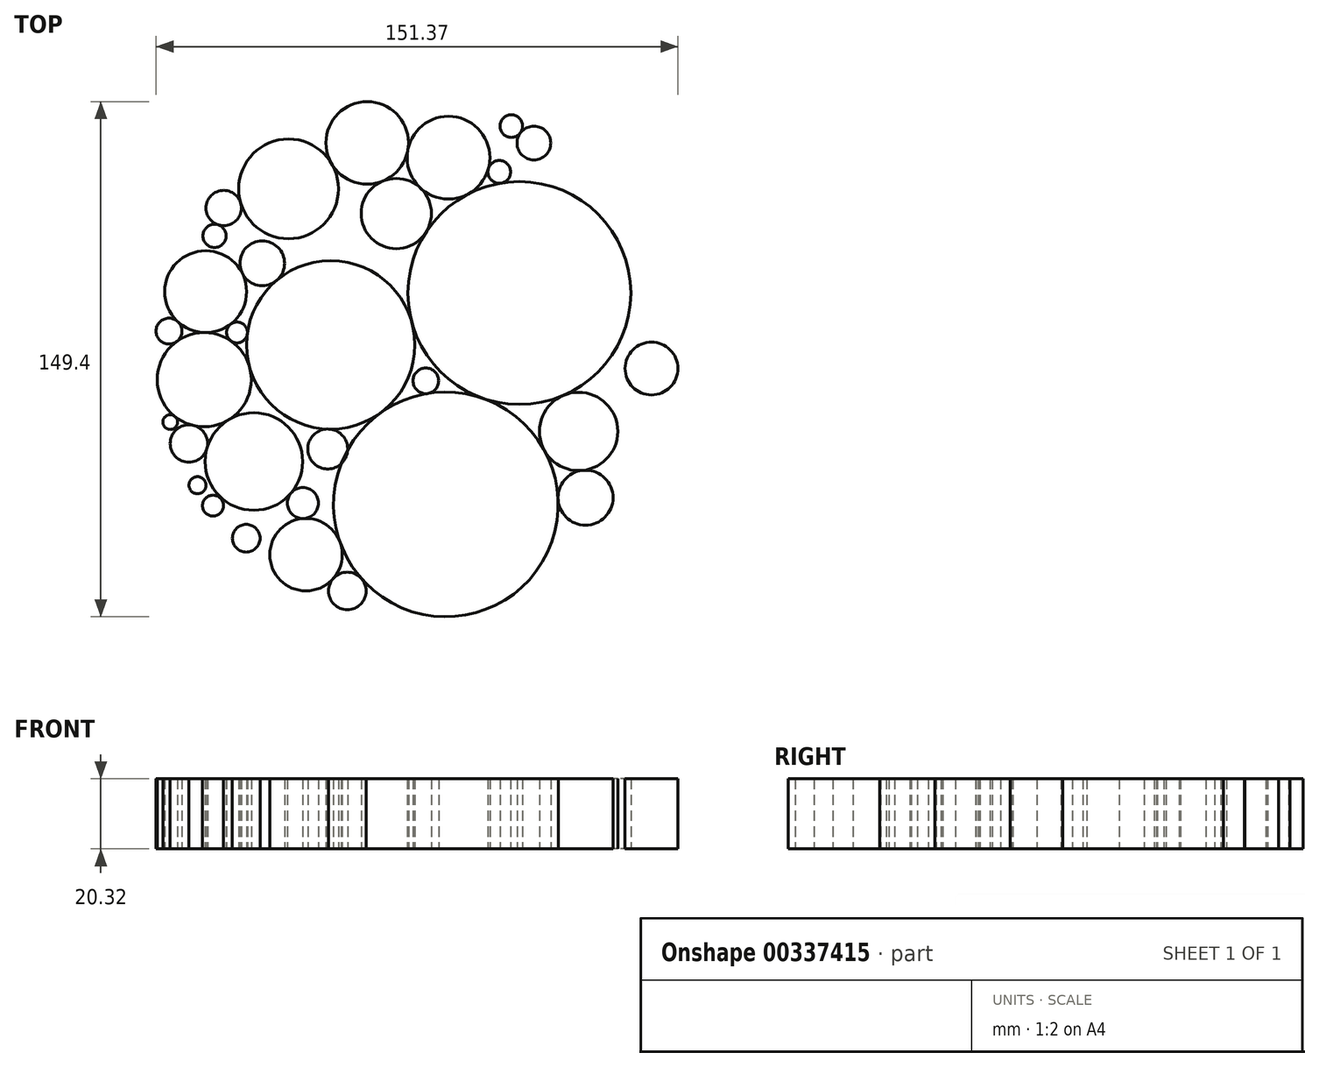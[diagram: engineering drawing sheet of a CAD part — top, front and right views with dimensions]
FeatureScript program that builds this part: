
annotation { "Feature Type Name" : "Feature", "Feature Type Description" : "" }
export const myFeature = defineFeature(function(context is Context, id is Id, definition is map)
    precondition{}
    {
        {
            var Q0;
            Q0=qCreatedBy(makeId("Top.planeOp"),FACE);
            var sketch = newSketch(context, id + "F0", { "sketchPlane" : qUnion([Q0])});
            skCircle(sketch, "E0", {"center": v(0, 0) * mm, "radius": 75.93 * mm});
            skCircle(sketch, "E1", {"center": v(-37.07, 49.03) * mm, "radius": 14.46 * mm});
            skCircle(sketch, "E2", {"center": v(-55.87, 43.47) * mm, "radius": 5.14 * mm});
            skCircle(sketch, "E3", {"center": v(-61.11, 19.2) * mm, "radius": 11.87 * mm});
            skCircle(sketch, "E4", {"center": v(-58.54, 35.4) * mm, "radius": 3.36 * mm});
            skCircle(sketch, "E5", {"center": v(-14.26, 62.36) * mm, "radius": 11.96 * mm});
            skCircle(sketch, "E6", {"center": v(29.88, 18.82) * mm, "radius": 32.32 * mm});
            skCircle(sketch, "E7", {"center": v(9.32, 58.1) * mm, "radius": 12 * mm});
            skCircle(sketch, "E8", {"center": v(34.08, 62.33) * mm, "radius": 4.9 * mm});
            skCircle(sketch, "E9", {"center": v(27.53, 67.23) * mm, "radius": 3.29 * mm});
            skCircle(sketch, "E10", {"center": v(24.05, 53.96) * mm, "radius": 3.3 * mm});
            skCircle(sketch, "E11", {"center": v(8.55, -42.49) * mm, "radius": 32.6 * mm});
            skCircle(sketch, "E12", {"center": v(47.06, -21.33) * mm, "radius": 11.35 * mm});
            skCircle(sketch, "E13", {"center": v(49.07, -40.55) * mm, "radius": 7.98 * mm});
            skCircle(sketch, "E14", {"center": v(68.2, -3.07) * mm, "radius": 7.66 * mm});
            skCircle(sketch, "E15", {"center": v(-61.53, -6.3) * mm, "radius": 13.64 * mm});
            skCircle(sketch, "E16", {"center": v(-47.13, -30.05) * mm, "radius": 14.14 * mm});
            skCircle(sketch, "E17", {"center": v(-66, -24.83) * mm, "radius": 5.42 * mm});
            skCircle(sketch, "E18", {"center": v(-24.84, 3.79) * mm, "radius": 24.42 * mm});
            skCircle(sketch, "E19", {"center": v(-5.83, 41.88) * mm, "radius": 10.19 * mm});
            skCircle(sketch, "E20", {"center": v(-44.71, 27.45) * mm, "radius": 6.48 * mm});
            skCircle(sketch, "E21", {"center": v(-25.7, -26.41) * mm, "radius": 5.8 * mm});
            skCircle(sketch, "E22", {"center": v(2.74, -6.64) * mm, "radius": 3.72 * mm});
            skCircle(sketch, "E23", {"center": v(-32.9, -42.1) * mm, "radius": 4.5 * mm});
            skCircle(sketch, "E24", {"center": v(-32, -57.07) * mm, "radius": 10.5 * mm});
            skCircle(sketch, "E25", {"center": v(-49.36, -52.3) * mm, "radius": 4.02 * mm});
            skCircle(sketch, "E26", {"center": v(-58.99, -42.83) * mm, "radius": 3.03 * mm});
            skCircle(sketch, "E27", {"center": v(-63.5, -36.92) * mm, "radius": 2.47 * mm});
            skCircle(sketch, "E28", {"center": v(-71.4, -18.6) * mm, "radius": 2.14 * mm});
            skCircle(sketch, "E29", {"center": v(-71.76, 7.77) * mm, "radius": 3.75 * mm});
            skCircle(sketch, "E30", {"center": v(-52.04, 7.4) * mm, "radius": 3.02 * mm});
            skCircle(sketch, "E31", {"center": v(-20.03, -67.59) * mm, "radius": 5.44 * mm});
            skCircle(sketch, "E32", {"center": v(14.35, -71.34) * mm, "radius": 3.16 * mm});
            skSolve(sketch);
        }
        {
            var Q0;
            Q0=makeQuery(id+"F0.imprint","IMPRINT",FACE,{"disambiguationData":[TD([[makeQuery(id+"F0.imprint","IMPRINT",EDGE,{"derivedFrom":sQuery(id+"F0.wireOp",EDGE,"E14")}),1.0]])]});
            var Q1;
            Q1=makeQuery(id+"F0.imprint","IMPRINT",FACE,{"disambiguationData":[TD([[makeQuery(id+"F0.imprint","IMPRINT",EDGE,{"derivedFrom":sQuery(id+"F0.wireOp",EDGE,"E25")}),1.0]])]});
            var Q2;
            Q2=makeQuery(id+"F0.imprint","IMPRINT",FACE,{"disambiguationData":[TD([[makeQuery(id+"F0.imprint","IMPRINT",EDGE,{"derivedFrom":sQuery(id+"F0.wireOp",EDGE,"E26")}),1.0]])]});
            var Q3;
            Q3=makeQuery(id+"F0.imprint","IMPRINT",FACE,{"disambiguationData":[TD([[makeQuery(id+"F0.imprint","IMPRINT",EDGE,{"derivedFrom":sQuery(id+"F0.wireOp",EDGE,"E27")}),1.0]])]});
            var Q4;
            Q4=makeQuery(id+"F0.imprint","IMPRINT",FACE,{"disambiguationData":[TD([[makeQuery(id+"F0.imprint","IMPRINT",EDGE,{"derivedFrom":sQuery(id+"F0.wireOp",EDGE,"E32")}),1.0]])]});
            var Q5;
            {var subQ0=sQuery(id+"F0.wireOp",EDGE,"E2");var subQ1=makeQuery(id+"F0.imprint","INTERSECT",VERTEX,{"derivedFrom":[sQuery(id+"F0.wireOp",EDGE,"E0"),subQ0]});Q5=makeQuery(id+"F0.imprint","IMPRINT",FACE,{"disambiguationData":[TD([[makeQuery(id+"F0.imprint","IMPRINT",EDGE,{"disambiguationData":[TD([[subQ1,1.0]])],"derivedFrom":subQ0}),1.0]])]});}
            var Q6;
            {var subQ0=sQuery(id+"F0.wireOp",EDGE,"E8");var subQ1=makeQuery(id+"F0.imprint","INTERSECT",VERTEX,{"derivedFrom":[sQuery(id+"F0.wireOp",EDGE,"E0"),subQ0]});Q6=makeQuery(id+"F0.imprint","IMPRINT",FACE,{"disambiguationData":[TD([[makeQuery(id+"F0.imprint","IMPRINT",EDGE,{"disambiguationData":[TD([[subQ1,-1.0]])],"derivedFrom":subQ0}),1.0]])]});}
            var Q7;
            {var subQ0=sQuery(id+"F0.wireOp",EDGE,"E9");var subQ1=makeQuery(id+"F0.imprint","INTERSECT",VERTEX,{"derivedFrom":[sQuery(id+"F0.wireOp",EDGE,"E0"),subQ0]});Q7=makeQuery(id+"F0.imprint","IMPRINT",FACE,{"disambiguationData":[TD([[makeQuery(id+"F0.imprint","IMPRINT",EDGE,{"disambiguationData":[TD([[subQ1,-1.0]])],"derivedFrom":subQ0}),1.0]])]});}
            var Q8;
            {var subQ0=sQuery(id+"F0.wireOp",EDGE,"E28");var subQ1=makeQuery(id+"F0.imprint","INTERSECT",VERTEX,{"derivedFrom":[sQuery(id+"F0.wireOp",EDGE,"E0"),subQ0]});Q8=makeQuery(id+"F0.imprint","IMPRINT",FACE,{"disambiguationData":[TD([[makeQuery(id+"F0.imprint","IMPRINT",EDGE,{"disambiguationData":[TD([[subQ1,1.0]])],"derivedFrom":subQ0}),1.0]])]});}
            var Q9;
            {var subQ0=sQuery(id+"F0.wireOp",EDGE,"E1");var subQ1=makeQuery(id+"F0.imprint","INTERSECT",VERTEX,{"derivedFrom":[sQuery(id+"F0.wireOp",EDGE,"E0"),subQ0]});Q9=makeQuery(id+"F0.imprint","IMPRINT",FACE,{"disambiguationData":[TD([[makeQuery(id+"F0.imprint","IMPRINT",EDGE,{"disambiguationData":[TD([[subQ1,1.0]])],"derivedFrom":subQ0}),1.0]])]});}
            var Q10;
            {var subQ0=sQuery(id+"F0.wireOp",EDGE,"E17");var subQ1=makeQuery(id+"F0.imprint","INTERSECT",VERTEX,{"derivedFrom":[sQuery(id+"F0.wireOp",EDGE,"E0"),subQ0]});Q10=makeQuery(id+"F0.imprint","IMPRINT",FACE,{"disambiguationData":[TD([[makeQuery(id+"F0.imprint","IMPRINT",EDGE,{"disambiguationData":[TD([[subQ1,1.0]])],"derivedFrom":subQ0}),1.0]])]});}
            var Q11;
            {var subQ0=sQuery(id+"F0.wireOp",EDGE,"E29");var subQ1=makeQuery(id+"F0.imprint","INTERSECT",VERTEX,{"derivedFrom":[sQuery(id+"F0.wireOp",EDGE,"E0"),subQ0]});Q11=makeQuery(id+"F0.imprint","IMPRINT",FACE,{"disambiguationData":[TD([[makeQuery(id+"F0.imprint","IMPRINT",EDGE,{"disambiguationData":[TD([[subQ1,1.0]])],"derivedFrom":subQ0}),1.0]])]});}
            var Q12;
            {var subQ0=sQuery(id+"F0.wireOp",EDGE,"E31");var subQ1=makeQuery(id+"F0.imprint","INTERSECT",VERTEX,{"derivedFrom":[sQuery(id+"F0.wireOp",EDGE,"E11"),subQ0]});Q12=makeQuery(id+"F0.imprint","IMPRINT",FACE,{"disambiguationData":[TD([[makeQuery(id+"F0.imprint","IMPRINT",EDGE,{"disambiguationData":[TD([[subQ1,-1.0]])],"derivedFrom":subQ0}),1.0]])]});}
            var Q13;
            {var subQ0=sQuery(id+"F0.wireOp",EDGE,"E5");var subQ1=makeQuery(id+"F0.imprint","INTERSECT",VERTEX,{"derivedFrom":[sQuery(id+"F0.wireOp",EDGE,"E0"),subQ0]});Q13=makeQuery(id+"F0.imprint","IMPRINT",FACE,{"disambiguationData":[TD([[makeQuery(id+"F0.imprint","IMPRINT",EDGE,{"disambiguationData":[TD([[subQ1,-1.0]])],"derivedFrom":subQ0}),1.0]])]});}
            var Q14;
            {var subQ0=sQuery(id+"F0.wireOp",EDGE,"E24");var subQ1=makeQuery(id+"F0.imprint","INTERSECT",VERTEX,{"derivedFrom":[sQuery(id+"F0.wireOp",EDGE,"E11"),subQ0]});Q14=makeQuery(id+"F0.imprint","IMPRINT",FACE,{"disambiguationData":[TD([[makeQuery(id+"F0.imprint","IMPRINT",EDGE,{"disambiguationData":[TD([[subQ1,-1.0]])],"derivedFrom":subQ0}),1.0]])]});}
            var Q15;
            {var subQ0=sQuery(id+"F0.wireOp",EDGE,"E3");var subQ4=makeQuery(id+"F0.imprint","INTERSECT",VERTEX,{"derivedFrom":[sQuery(id+"F0.wireOp",EDGE,"E0"),subQ0]});Q15=makeQuery(id+"F0.imprint","IMPRINT",FACE,{"disambiguationData":[TD([[makeQuery(id+"F0.imprint","IMPRINT",EDGE,{"disambiguationData":[TD([[subQ4,1.0]])],"derivedFrom":subQ0}),1.0]])]});}
            var Q16;
            {var subQ10=sQuery(id+"F0.wireOp",EDGE,"E32");Q16=makeQuery(id+"F0.imprint","IMPRINT",FACE,{"disambiguationData":[TD([[makeQuery(id+"F0.imprint","IMPRINT",EDGE,{"derivedFrom":subQ10}),-1.0]])]});}
            var Q17;
            {var subQ0=sQuery(id+"F0.wireOp",EDGE,"E20");var subQ1=makeQuery(id+"F0.imprint","INTERSECT",VERTEX,{"derivedFrom":[sQuery(id+"F0.wireOp",EDGE,"E3"),subQ0]});Q17=makeQuery(id+"F0.imprint","IMPRINT",FACE,{"disambiguationData":[TD([[makeQuery(id+"F0.imprint","IMPRINT",EDGE,{"disambiguationData":[TD([[subQ1,-1.0]])],"derivedFrom":subQ0}),1.0]])]});}
            var Q18;
            Q18=makeQuery(id+"F0.imprint","IMPRINT",FACE,{"disambiguationData":[TD([[makeQuery(id+"F0.imprint","IMPRINT",EDGE,{"derivedFrom":sQuery(id+"F0.wireOp",EDGE,"E4")}),1.0]])]});
            var Q19;
            {var subQ0=sQuery(id+"F0.wireOp",EDGE,"E19");var subQ1=makeQuery(id+"F0.imprint","INTERSECT",VERTEX,{"derivedFrom":[sQuery(id+"F0.wireOp",EDGE,"E5"),subQ0]});Q19=makeQuery(id+"F0.imprint","IMPRINT",FACE,{"disambiguationData":[TD([[makeQuery(id+"F0.imprint","IMPRINT",EDGE,{"disambiguationData":[TD([[subQ1,1.0]])],"derivedFrom":subQ0}),1.0]])]});}
            var Q20;
            {var subQ0=sQuery(id+"F0.wireOp",EDGE,"E7");var subQ1=makeQuery(id+"F0.imprint","INTERSECT",VERTEX,{"derivedFrom":[sQuery(id+"F0.wireOp",EDGE,"E5"),subQ0]});Q20=makeQuery(id+"F0.imprint","IMPRINT",FACE,{"disambiguationData":[TD([[makeQuery(id+"F0.imprint","IMPRINT",EDGE,{"disambiguationData":[TD([[subQ1,-1.0]])],"derivedFrom":subQ0}),1.0]])]});}
            var Q21;
            {var subQ0=sQuery(id+"F0.wireOp",EDGE,"E15");var subQ4=makeQuery(id+"F0.imprint","INTERSECT",VERTEX,{"derivedFrom":[subQ0,sQuery(id+"F0.wireOp",EDGE,"E30")]});Q21=makeQuery(id+"F0.imprint","IMPRINT",FACE,{"disambiguationData":[TD([[makeQuery(id+"F0.imprint","IMPRINT",EDGE,{"disambiguationData":[TD([[subQ4,1.0]])],"derivedFrom":subQ0}),1.0]])]});}
            var Q22;
            {var subQ0=sQuery(id+"F0.wireOp",EDGE,"E30");var subQ1=makeQuery(id+"F0.imprint","INTERSECT",VERTEX,{"derivedFrom":[sQuery(id+"F0.wireOp",EDGE,"E3"),subQ0]});Q22=makeQuery(id+"F0.imprint","IMPRINT",FACE,{"disambiguationData":[TD([[makeQuery(id+"F0.imprint","IMPRINT",EDGE,{"disambiguationData":[TD([[subQ1,-1.0]])],"derivedFrom":subQ0}),1.0]])]});}
            var Q23;
            {var subQ0=sQuery(id+"F0.wireOp",EDGE,"E18");var subQ5=makeQuery(id+"F0.imprint","INTERSECT",VERTEX,{"derivedFrom":[sQuery(id+"F0.wireOp",EDGE,"E6"),subQ0]});Q23=makeQuery(id+"F0.imprint","IMPRINT",FACE,{"disambiguationData":[TD([[makeQuery(id+"F0.imprint","IMPRINT",EDGE,{"disambiguationData":[TD([[subQ5,-1.0]])],"derivedFrom":subQ0}),1.0]])]});}
            var Q24;
            {var subQ0=sQuery(id+"F0.wireOp",EDGE,"E16");var subQ1=makeQuery(id+"F0.imprint","INTERSECT",VERTEX,{"derivedFrom":[sQuery(id+"F0.wireOp",EDGE,"E15"),subQ0]});Q24=makeQuery(id+"F0.imprint","IMPRINT",FACE,{"disambiguationData":[TD([[makeQuery(id+"F0.imprint","IMPRINT",EDGE,{"disambiguationData":[TD([[subQ1,-1.0]])],"derivedFrom":subQ0}),1.0]])]});}
            var Q25;
            {var subQ0=sQuery(id+"F0.wireOp",EDGE,"E21");var subQ1=sQuery(id+"F0.wireOp",EDGE,"E11");var subQ2=makeQuery(id+"F0.imprint","INTERSECT",VERTEX,{"disambiguationData":[OD(0.0)],"derivedFrom":[subQ1,subQ0]});Q25=makeQuery(id+"F0.imprint","IMPRINT",FACE,{"disambiguationData":[TD([[makeQuery(id+"F0.imprint","IMPRINT",EDGE,{"disambiguationData":[TD([[subQ2,-1.0]])],"derivedFrom":subQ1}),-1.0]])]});}
            var Q26;
            {var subQ0=sQuery(id+"F0.wireOp",EDGE,"E23");var subQ1=makeQuery(id+"F0.imprint","INTERSECT",VERTEX,{"derivedFrom":[sQuery(id+"F0.wireOp",EDGE,"E16"),subQ0]});Q26=makeQuery(id+"F0.imprint","IMPRINT",FACE,{"disambiguationData":[TD([[makeQuery(id+"F0.imprint","IMPRINT",EDGE,{"disambiguationData":[TD([[subQ1,-1.0]])],"derivedFrom":subQ0}),1.0]])]});}
            var Q27;
            {var subQ0=sQuery(id+"F0.wireOp",EDGE,"E6");var subQ4=makeQuery(id+"F0.imprint","INTERSECT",VERTEX,{"derivedFrom":[subQ0,sQuery(id+"F0.wireOp",EDGE,"E7")]});Q27=makeQuery(id+"F0.imprint","IMPRINT",FACE,{"disambiguationData":[TD([[makeQuery(id+"F0.imprint","IMPRINT",EDGE,{"disambiguationData":[TD([[subQ4,1.0]])],"derivedFrom":subQ0}),1.0]])]});}
            var Q28;
            Q28=makeQuery(id+"F0.imprint","IMPRINT",FACE,{"disambiguationData":[TD([[makeQuery(id+"F0.imprint","IMPRINT",EDGE,{"derivedFrom":sQuery(id+"F0.wireOp",EDGE,"E22")}),1.0]])]});
            var Q29;
            {var subQ0=sQuery(id+"F0.wireOp",EDGE,"E12");var subQ1=makeQuery(id+"F0.imprint","INTERSECT",VERTEX,{"derivedFrom":[sQuery(id+"F0.wireOp",EDGE,"E6"),subQ0]});Q29=makeQuery(id+"F0.imprint","IMPRINT",FACE,{"disambiguationData":[TD([[makeQuery(id+"F0.imprint","IMPRINT",EDGE,{"disambiguationData":[TD([[subQ1,-1.0]])],"derivedFrom":subQ0}),1.0]])]});}
            var Q30;
            {var subQ0=sQuery(id+"F0.wireOp",EDGE,"E13");var subQ1=makeQuery(id+"F0.imprint","INTERSECT",VERTEX,{"derivedFrom":[sQuery(id+"F0.wireOp",EDGE,"E11"),subQ0]});Q30=makeQuery(id+"F0.imprint","IMPRINT",FACE,{"disambiguationData":[TD([[makeQuery(id+"F0.imprint","IMPRINT",EDGE,{"disambiguationData":[TD([[subQ1,1.0]])],"derivedFrom":subQ0}),1.0]])]});}
            var Q31;
            {var subQ0=sQuery(id+"F0.wireOp",EDGE,"E10");var subQ1=makeQuery(id+"F0.imprint","INTERSECT",VERTEX,{"derivedFrom":[sQuery(id+"F0.wireOp",EDGE,"E6"),subQ0]});Q31=makeQuery(id+"F0.imprint","IMPRINT",FACE,{"disambiguationData":[TD([[makeQuery(id+"F0.imprint","IMPRINT",EDGE,{"disambiguationData":[TD([[subQ1,1.0]])],"derivedFrom":subQ0}),1.0]])]});}
            extrude(context, id + "F1", {"entities" : qUnion([Q0, Q1, Q2, Q3, Q4, Q5, Q6, Q7, Q8, Q9, Q10, Q11, Q12, Q13, Q14, Q15, Q16, Q17, Q18, Q19, Q20, Q21, Q22, Q23, Q24, Q25, Q26, Q27, Q28, Q29, Q30, Q31]), "depth" : 20.32 * mm});
        }
    });
